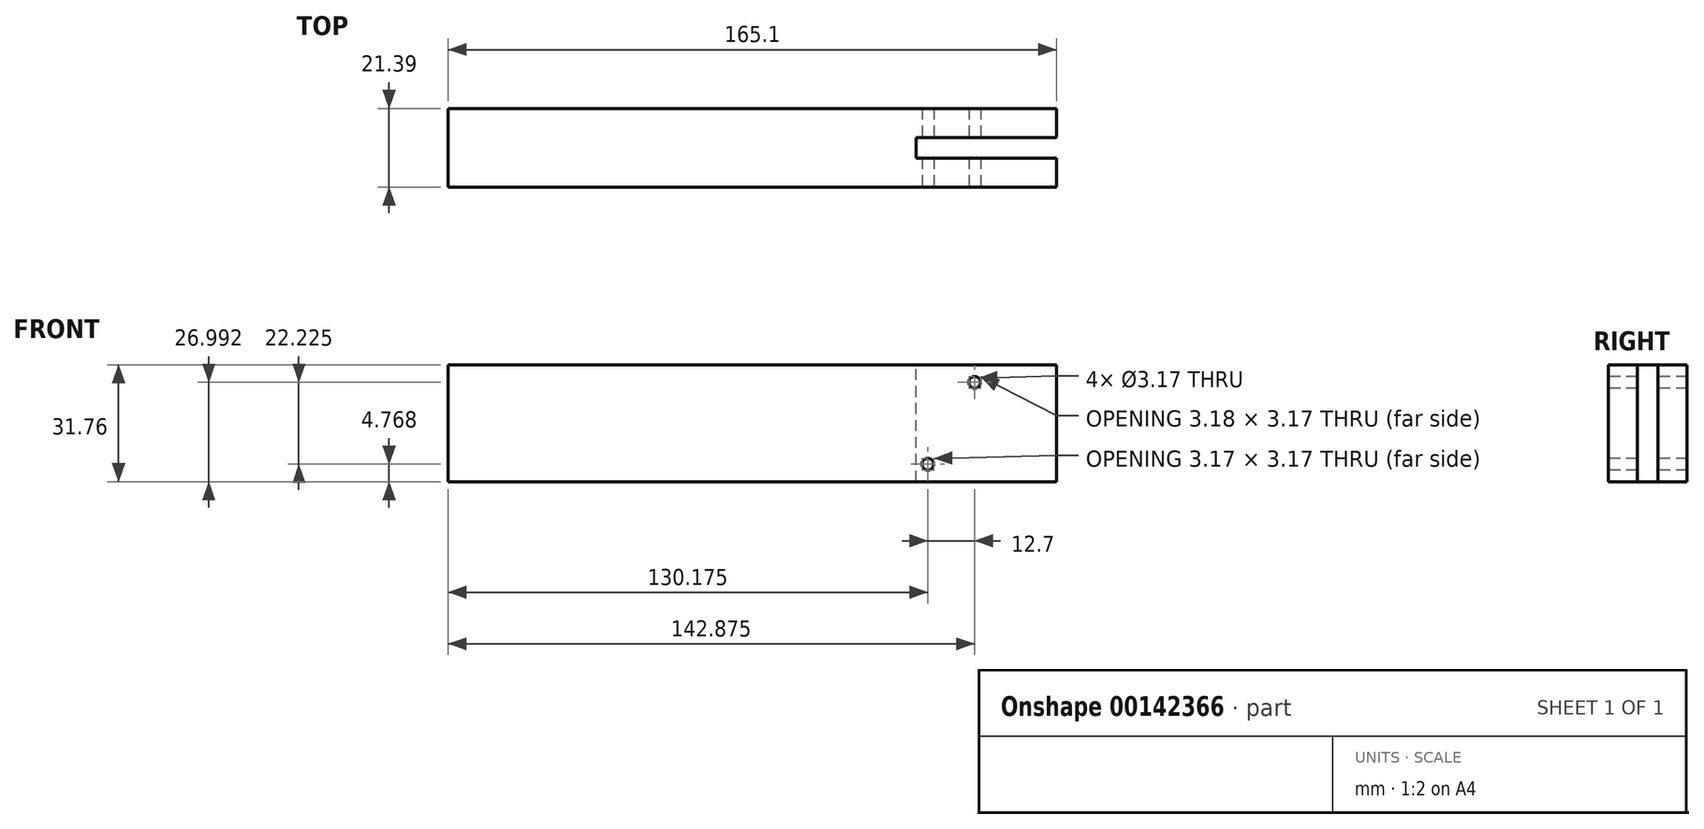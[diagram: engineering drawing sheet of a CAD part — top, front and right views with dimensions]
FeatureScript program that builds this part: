
annotation { "Feature Type Name" : "Feature", "Feature Type Description" : "" }
export const myFeature = defineFeature(function(context is Context, id is Id, definition is map)
    precondition{}
    {
        {
            var Q0;
            Q0=qCreatedBy(makeId("Front.planeOp"),FACE);
            var sketch = newSketch(context, id + "F0", { "sketchPlane" : qUnion([Q0])});
            skLineSegment(sketch, "E0.bottom", {"start": v(-82.55, 15.88) * mm, "end": v(82.55, 15.88) * mm});
            skLineSegment(sketch, "E0.top", {"start": v(-82.55, -15.88) * mm, "end": v(82.55, -15.88) * mm});
            skLineSegment(sketch, "E0.left", {"start": v(-82.55, 15.88) * mm, "end": v(-82.55, -15.88) * mm});
            skLineSegment(sketch, "E0.right", {"start": v(82.55, 15.88) * mm, "end": v(82.55, -15.88) * mm});
            skPoint(sketch, "E0.middle", {"position": v(0, 0) * mm});
            skSolve(sketch);
        }
        {
            var Q0;
            Q0 = qSketchRegion(id + "F0", true);
            extrude(context, id + "F1", {"entities" : qUnion([Q0]), "depth" : 21.4 * mm});
        }
        {
            var Q0;
            Q0=makeQuery(id+"F1.opExtrude","SWEPT_FACE",FACE,{"disambiguationData":[OSD([sQuery(id+"F0.wireOp",EDGE,"E0.bottom")])]});
            var sketch = newSketch(context, id + "F2", { "sketchPlane" : qUnion([Q0])});
            skLineSegment(sketch, "E1.bottom", {"start": v(82.55, -7.92) * mm, "end": v(44.45, -7.92) * mm});
            skLineSegment(sketch, "E1.top", {"start": v(82.55, -13.47) * mm, "end": v(44.45, -13.47) * mm});
            skLineSegment(sketch, "E1.left", {"start": v(82.55, -7.92) * mm, "end": v(82.55, -13.47) * mm});
            skLineSegment(sketch, "E1.right", {"start": v(44.45, -7.92) * mm, "end": v(44.45, -13.47) * mm});
            skPoint(sketch, "E2", {"position": v(82.55, -10.7) * mm});
            skSolve(sketch);
        }
        {
            var Q0;
            Q0 = qSketchRegion(id + "F2", true);
            var Q1;
            Q1=makeQuery(id+"F1.opExtrude","SWEPT_FACE",FACE,{"disambiguationData":[OSD([sQuery(id+"F0.wireOp",EDGE,"E0.top")])]});
            extrude(context, id + "F3", {"entities" : qUnion([Q0]), "operationType" : NewBodyOperationType.REMOVE, "endBound" : BoundingType.UP_TO_SURFACE, "oppositeDirection" : true, "endBoundEntityFace" : qUnion([Q1]), "depth" : 25.4 * mm});
        }
        {
            var Q0;
            Q0=makeQuery(id+"F1.opExtrude","CAP_FACE",FACE,{"disambiguationData":[OSD([sQuery(id+"F0.wireOp",EDGE,"E0.bottom"),sQuery(id+"F0.wireOp",EDGE,"E0.top"),sQuery(id+"F0.wireOp",EDGE,"E0.left"),sQuery(id+"F0.wireOp",EDGE,"E0.right")])],"isStart":false});
            var sketch = newSketch(context, id + "F4", { "sketchPlane" : qUnion([Q0])});
            skCircle(sketch, "E3", {"center": v(60.33, 11.11) * mm, "radius": 1.59 * mm});
            skCircle(sketch, "E4", {"center": v(47.62, -11.11) * mm, "radius": 1.59 * mm});
            skSolve(sketch);
        }
        {
            var Q0;
            Q0 = qSketchRegion(id + "F4", true);
            var Q1;
            Q1=makeQuery(id+"F1.opExtrude","CAP_FACE",FACE,{"disambiguationData":[OSD([sQuery(id+"F0.wireOp",EDGE,"E0.bottom"),sQuery(id+"F0.wireOp",EDGE,"E0.top"),sQuery(id+"F0.wireOp",EDGE,"E0.left"),sQuery(id+"F0.wireOp",EDGE,"E0.right")])],"isStart":true});
            extrude(context, id + "F5", {"entities" : qUnion([Q0]), "operationType" : NewBodyOperationType.REMOVE, "endBound" : BoundingType.UP_TO_SURFACE, "oppositeDirection" : true, "endBoundEntityFace" : qUnion([Q1]), "depth" : 25.4 * mm});
        }
    });
